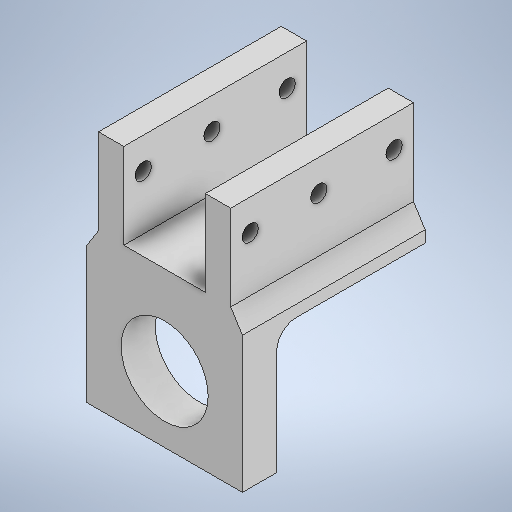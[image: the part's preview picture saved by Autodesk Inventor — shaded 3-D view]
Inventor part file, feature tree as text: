
AUTODESK INVENTOR PART (.ipt)
format: ipt  version: 2025.1 (Build 291241020, 241B)  size: 413,696 bytes
history: native  units: in
note: dims shown in document units (in); Inventor stores cm internally (conversion verified against a paired STEP export)
features: projected_geometry x11, extrude x10, sketch x10, fillet x1
ambient origin geometry x8: Origin, YZ Plane, XZ Plane, XY Plane, X Axis, Y Axis, Z Axis, Center Point
bodies: Solid1 (feature_tree)
feature tree (32):
  extrude  "Extrusion1"  Depth=2.0in
  extrude  "Extrusion3"  Depth=1.0in
  extrude  "Extrusion4"  Depth=0.35in TaperAngle=0.0deg
  extrude  "Extrusion5"  Depth=2.0in TaperAngle=0.0deg
  extrude  "Extrusion6"  Depth=1.05in
  extrude  "Extrusion7"  Depth=0.09in TaperAngle=0.0deg
  extrude  "Extrusion8"  Depth=1.465in TaperAngle=0.0deg
  extrude  "Extrusion9"  Depth=0.7in
  fillet  "Fillet4"  Radius=0.209in
  extrude  "Extrusion10"  Depth=0.25in
  extrude  "Extrusion11"  Depth=0.25in
  sketch  "Sketch1"  dims[d1=1.75in d2=2.0in]
  sketch  "Sketch3"  dims[d6=0.35in d7=1.0in]
  projected_geometry  "Projected Loop2"
  sketch  "Sketch5"  dims[d8=0.35in d9=0.35in d10=0.0in]
  projected_geometry  "Projected Loop3"
  sketch  "Sketch9"  dims[d13=1.12in d14=2.0in d15=0.0in]
  sketch  "Sketch11"  dims[d23=5.25in d24=0.0in d27=1.05in]
  projected_geometry  "Projected Loop8"
  projected_geometry  "Projected Loop9"
  sketch  "Sketch12"  dims[d28=1.6875in d29=0.0in d30=0.09in d31=0.0in]
  projected_geometry  "Projected Loop10"
  sketch  "Sketch13"  dims[d32=0.2225in d33=0.0in d34=1.465in d35=0.0in]
  sketch  "Sketch14"  dims[d36=1.84in d37=0.0in d39=0.7in d40=0.209in]
  projected_geometry  "Projected Loop11"
  projected_geometry  "Projected Loop12"
  projected_geometry  "Projected Loop13"
  sketch  "Sketch15"  dims[d41=0.25in d42=0.209in]
  projected_geometry  "Projected Loop14"
  sketch  "Sketch16"  dims[d43=0.25in d44=0.209in d45=0.25in d46=0.0in d47=0.24in d51=1.12in d52=1.14in d53=1.7in d54=1.3375in d55=0.0in d56=0.1in d57=0.0in]
  projected_geometry  "Projected Loop15"
  projected_geometry  "Projected Loop16"
